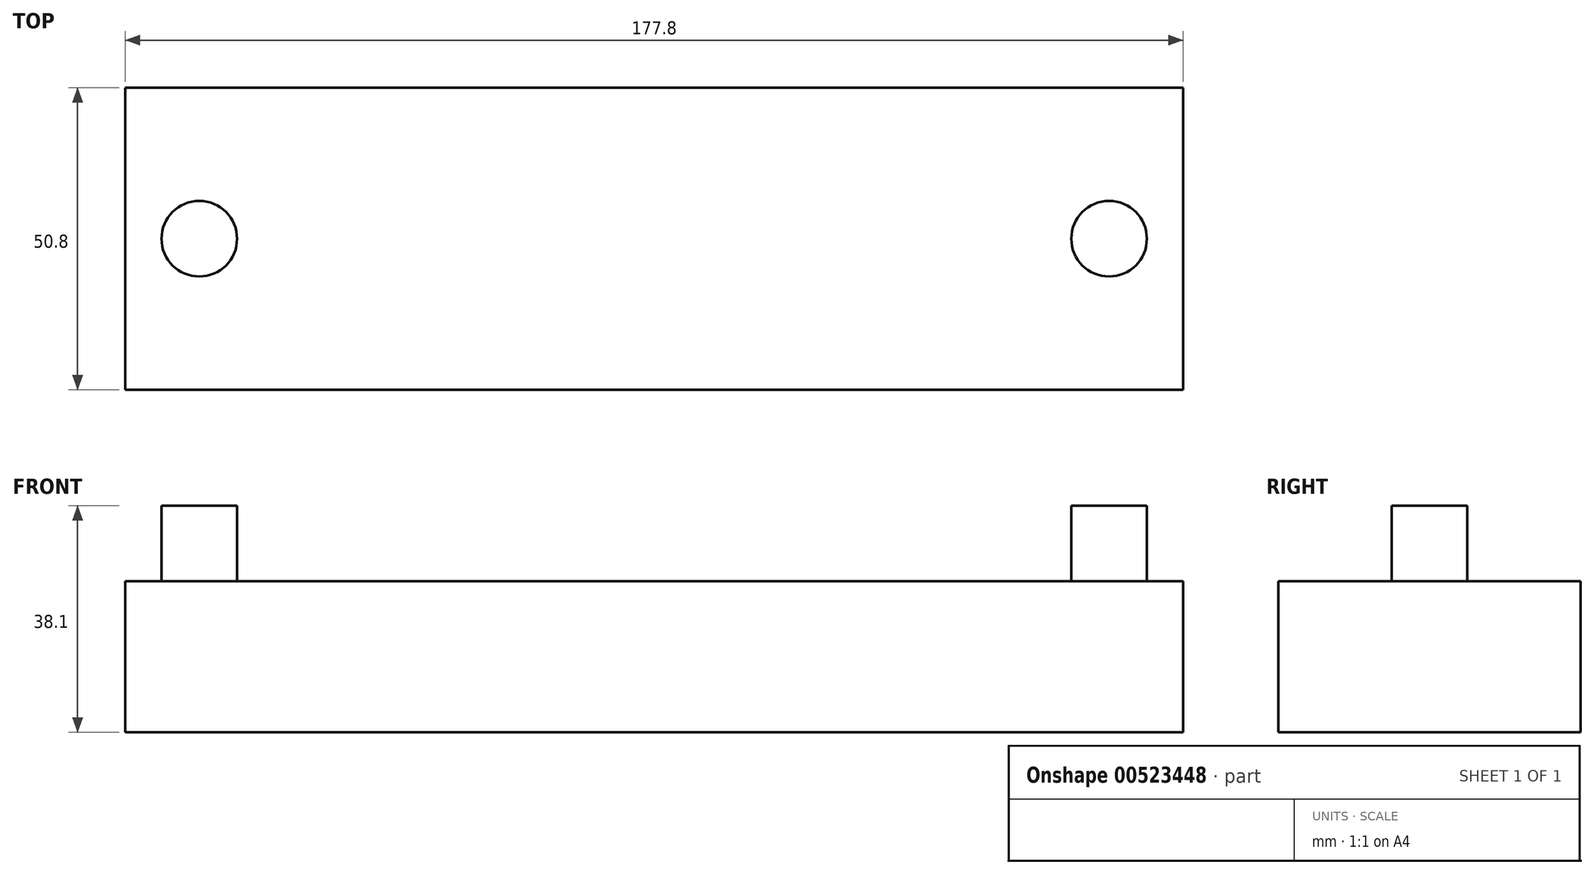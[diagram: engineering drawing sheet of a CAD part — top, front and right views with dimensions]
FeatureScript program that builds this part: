
annotation { "Feature Type Name" : "Feature", "Feature Type Description" : "" }
export const myFeature = defineFeature(function(context is Context, id is Id, definition is map)
    precondition{}
    {
        {
            var Q0;
            Q0=qCreatedBy(makeId("Top.planeOp"),FACE);
            var sketch = newSketch(context, id + "F0", { "sketchPlane" : qUnion([Q0])});
            skLineSegment(sketch, "E0.bottom", {"start": v(-88.9, 25.4) * mm, "end": v(88.9, 25.4) * mm});
            skLineSegment(sketch, "E0.top", {"start": v(-88.9, -25.4) * mm, "end": v(88.9, -25.4) * mm});
            skLineSegment(sketch, "E0.left", {"start": v(-88.9, 25.4) * mm, "end": v(-88.9, -25.4) * mm});
            skLineSegment(sketch, "E0.right", {"start": v(88.9, 25.4) * mm, "end": v(88.9, -25.4) * mm});
            skSolve(sketch);
        }
        {
            var Q0;
            Q0=makeQuery(id+"F0.imprint","IMPRINT",FACE,{"disambiguationData":[TD([[makeQuery(id+"F0.imprint","IMPRINT",EDGE,{"derivedFrom":sQuery(id+"F0.wireOp",EDGE,"E0.bottom")}),-1.0]])]});
            extrude(context, id + "F1", {"entities" : qUnion([Q0]), "depth" : 25.4 * mm, "offsetDistance" : 25.4 * mm});
        }
        {
            var Q0;
            Q0=makeQuery(id+"F1.opExtrude","CAP_FACE",FACE,{"disambiguationData":[OSD([sQuery(id+"F0.wireOp",EDGE,"E0.bottom"),sQuery(id+"F0.wireOp",EDGE,"E0.top"),sQuery(id+"F0.wireOp",EDGE,"E0.left"),sQuery(id+"F0.wireOp",EDGE,"E0.right")])],"isStart":false});
            var sketch = newSketch(context, id + "F2", { "sketchPlane" : qUnion([Q0])});
            skCircle(sketch, "E1", {"center": v(-76.45, 0) * mm, "radius": 6.35 * mm});
            skCircle(sketch, "E2.MirrorC", {"center": v(76.45, 0) * mm, "radius": 6.35 * mm});
            skSolve(sketch);
        }
        {
            var Q0;
            Q0 = qSketchRegion(id + "F2", true);
            extrude(context, id + "F3", {"entities" : qUnion([Q0]), "operationType" : NewBodyOperationType.ADD, "depth" : 12.7 * mm, "offsetDistance" : 25.4 * mm});
        }
    });
